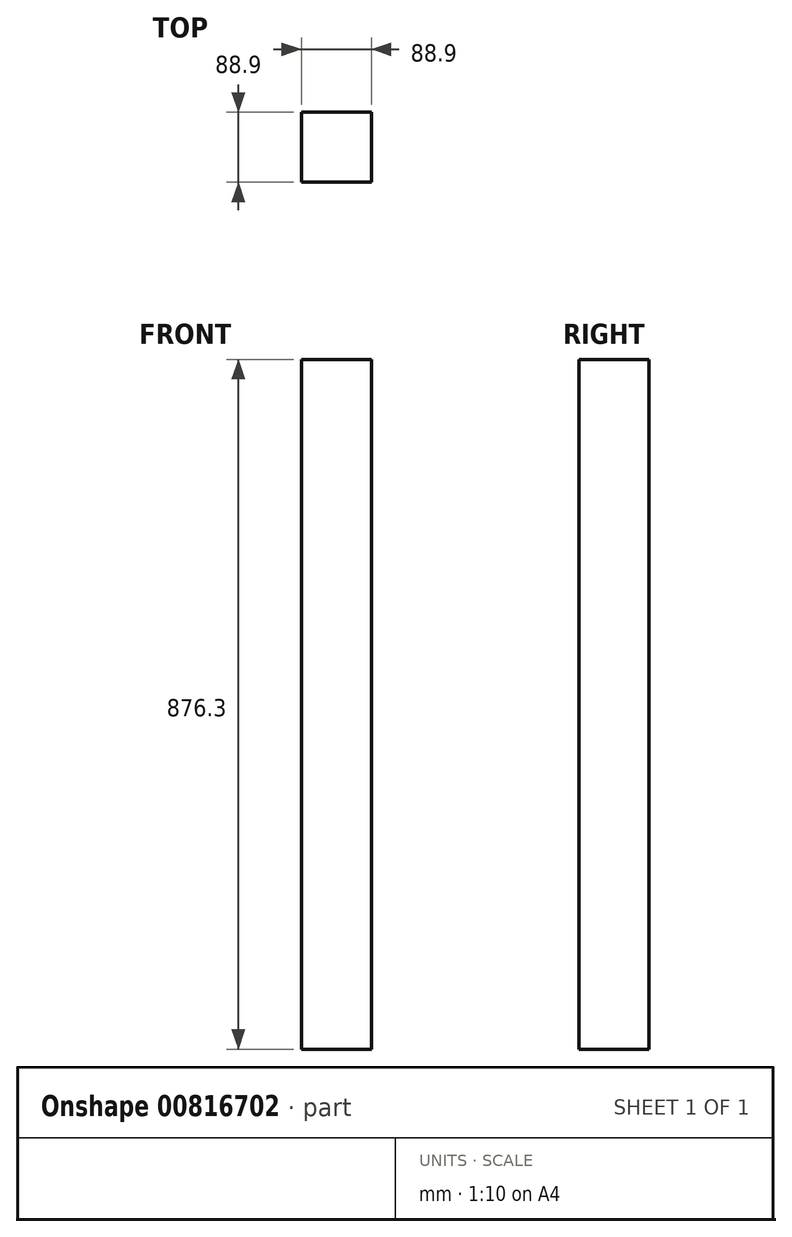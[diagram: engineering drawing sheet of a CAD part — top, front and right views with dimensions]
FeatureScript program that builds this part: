
annotation { "Feature Type Name" : "Feature", "Feature Type Description" : "" }
export const myFeature = defineFeature(function(context is Context, id is Id, definition is map)
    precondition{}
    {
        {
            var Q0;
            Q0=qCreatedBy(makeId("Top.planeOp"),FACE);
            var sketch = newSketch(context, id + "F0", { "sketchPlane" : qUnion([Q0])});
            skLineSegment(sketch, "E0.bottom", {"start": v(0, 0) * mm, "end": v(88.9, 0) * mm});
            skLineSegment(sketch, "E0.top", {"start": v(0, 88.9) * mm, "end": v(88.9, 88.9) * mm});
            skLineSegment(sketch, "E0.left", {"start": v(0, 0) * mm, "end": v(0, 88.9) * mm});
            skLineSegment(sketch, "E0.right", {"start": v(88.9, 0) * mm, "end": v(88.9, 88.9) * mm});
            skSolve(sketch);
        }
        {
            var Q0;
            Q0 = qSketchRegion(id + "F0", true);
            extrude(context, id + "F1", {"entities" : qUnion([Q0]), "depth" : 876.3 * mm, "offsetDistance" : 25.4 * mm});
        }
    });
